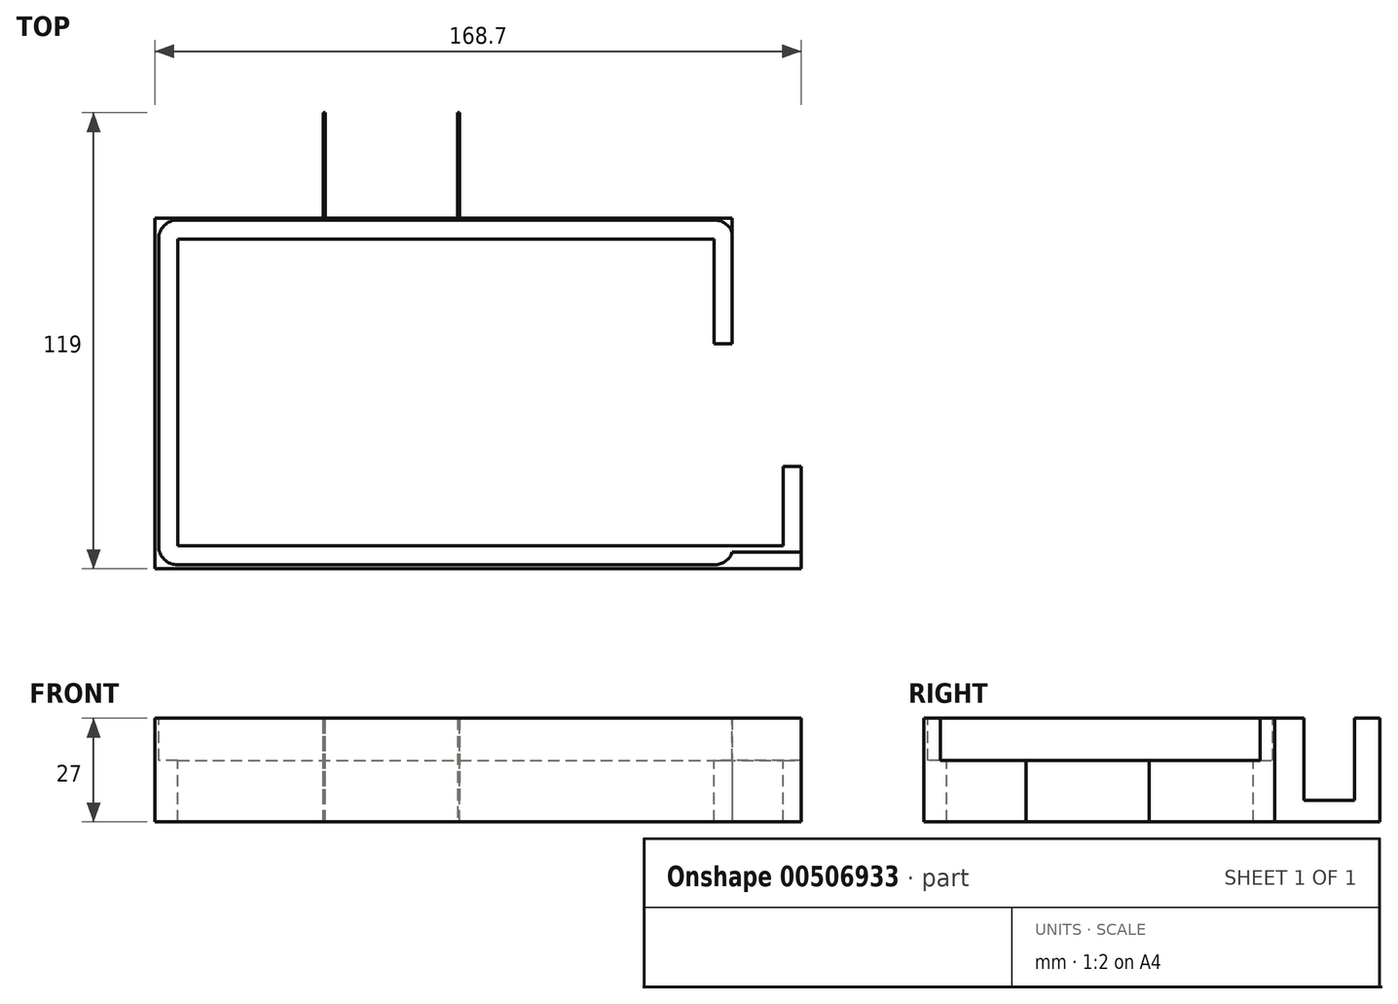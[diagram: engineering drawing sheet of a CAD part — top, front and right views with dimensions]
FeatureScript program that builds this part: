
annotation { "Feature Type Name" : "Feature", "Feature Type Description" : "" }
export const myFeature = defineFeature(function(context is Context, id is Id, definition is map)
    precondition{}
    {
        {
            var Q0;
            Q0=qCreatedBy(makeId("Top.planeOp"),FACE);
            var sketch = newSketch(context, id + "F0", { "sketchPlane" : qUnion([Q0])});
            skLineSegment(sketch, "E0.bottom", {"start": v(-95.15, 61.25) * mm, "end": v(74.85, 61.25) * mm});
            skLineSegment(sketch, "E0.top", {"start": v(-95.15, -68.75) * mm, "end": v(74.85, -68.75) * mm});
            skLineSegment(sketch, "E0.left", {"start": v(-95.15, 61.25) * mm, "end": v(-95.15, -68.75) * mm});
            skLineSegment(sketch, "E0.right", {"start": v(74.85, 61.25) * mm, "end": v(74.85, -68.75) * mm});
            skSolve(sketch);
        }
        {
            var Q0;
            Q0=makeQuery(id+"F0.imprint","IMPRINT",FACE,{"disambiguationData":[TD([[makeQuery(id+"F0.imprint","IMPRINT",EDGE,{"derivedFrom":sQuery(id+"F0.wireOp",EDGE,"E0.bottom")}),-1.0]])]});
            extrude(context, id + "F1", {"entities" : qUnion([Q0]), "depth" : 34 * mm});
        }
        {
            var Q0;
            Q0=makeQuery(id+"F1.opExtrude","CAP_FACE",FACE,{"disambiguationData":[OSD([sQuery(id+"F0.wireOp",EDGE,"E0.bottom"),sQuery(id+"F0.wireOp",EDGE,"E0.top"),sQuery(id+"F0.wireOp",EDGE,"E0.left"),sQuery(id+"F0.wireOp",EDGE,"E0.right")])],"isStart":false});
            shell(context, id + "F2", {"entities" : qUnion([Q0]), "thickness" : 1 * mm});
        }
        {
            var Q0;
            Q0=makeQuery(id+"F2.opShell","OFFSET_FACE",FACE,{"disambiguationData":[OSD([sQuery(id+"F0.wireOp",EDGE,"E0.bottom"),sQuery(id+"F0.wireOp",EDGE,"E0.top"),sQuery(id+"F0.wireOp",EDGE,"E0.left"),sQuery(id+"F0.wireOp",EDGE,"E0.right")])]});
            var sketch = newSketch(context, id + "F3", { "sketchPlane" : qUnion([Q0])});
            skLineSegment(sketch, "E1.bottom", {"start": v(-94.15, 60.25) * mm, "end": v(-50.65, 60.25) * mm});
            skLineSegment(sketch, "E1.top", {"start": v(-94.15, 22.25) * mm, "end": v(-50.65, 22.25) * mm});
            skLineSegment(sketch, "E1.left", {"start": v(-94.15, 60.25) * mm, "end": v(-94.15, 22.25) * mm});
            skLineSegment(sketch, "E1.right", {"start": v(-50.65, 60.25) * mm, "end": v(-50.65, 22.25) * mm});
            skSolve(sketch);
        }
        {
            var Q0;
            Q0=makeQuery(id+"F3.imprint","IMPRINT",FACE,{"disambiguationData":[TD([[makeQuery(id+"F3.imprint","IMPRINT",EDGE,{"derivedFrom":sQuery(id+"F3.wireOp",EDGE,"E1.bottom")}),-1.0]])]});
            extrude(context, id + "F4", {"entities" : qUnion([Q0]), "operationType" : NewBodyOperationType.ADD, "depth" : 32 * mm});
        }
        {
            var Q0;
            Q0=makeQuery(id+"F4.opExtrude","CAP_FACE",FACE,{"disambiguationData":[OSD([sQuery(id+"F3.wireOp",EDGE,"E1.bottom"),sQuery(id+"F3.wireOp",EDGE,"E1.top"),sQuery(id+"F3.wireOp",EDGE,"E1.left"),sQuery(id+"F3.wireOp",EDGE,"E1.right")])],"isStart":false});
            shell(context, id + "F5", {"entities" : qUnion([Q0]), "thickness" : 0.5 * mm});
        }
        {
            var Q0;
            Q0=makeQuery(id+"F2.opShell","OFFSET_FACE",FACE,{"disambiguationData":[OSD([sQuery(id+"F0.wireOp",EDGE,"E0.bottom"),sQuery(id+"F0.wireOp",EDGE,"E0.top"),sQuery(id+"F0.wireOp",EDGE,"E0.left"),sQuery(id+"F0.wireOp",EDGE,"E0.right")])]});
            var sketch = newSketch(context, id + "F6", { "sketchPlane" : qUnion([Q0])});
            skLineSegment(sketch, "E2.bottom", {"start": v(-50.65, 22.25) * mm, "end": v(-15.65, 22.25) * mm});
            skLineSegment(sketch, "E2.top", {"start": v(-50.65, 60.25) * mm, "end": v(-15.65, 60.25) * mm});
            skLineSegment(sketch, "E2.left", {"start": v(-50.65, 22.25) * mm, "end": v(-50.65, 60.25) * mm});
            skLineSegment(sketch, "E2.right", {"start": v(-15.65, 22.25) * mm, "end": v(-15.65, 60.25) * mm});
            skSolve(sketch);
        }
        {
            var Q0;
            Q0=makeQuery(id+"F6.imprint","IMPRINT",FACE,{"disambiguationData":[TD([[makeQuery(id+"F6.imprint","IMPRINT",EDGE,{"derivedFrom":sQuery(id+"F6.wireOp",EDGE,"E2.bottom")}),1.0]])]});
            extrude(context, id + "F7", {"entities" : qUnion([Q0]), "operationType" : NewBodyOperationType.ADD, "depth" : 32 * mm});
        }
        {
            var Q0;
            Q0=makeQuery(id+"F7.boolean.opBoolean","MERGE",FACE,{"derivedFrom":[makeQuery(id+"F4.opExtrude","CAP_FACE",FACE,{"disambiguationData":[OSD([sQuery(id+"F3.wireOp",EDGE,"E1.bottom"),sQuery(id+"F3.wireOp",EDGE,"E1.top"),sQuery(id+"F3.wireOp",EDGE,"E1.left"),sQuery(id+"F3.wireOp",EDGE,"E1.right")])],"isStart":false}),makeQuery(id+"F7.opExtrude","CAP_FACE",FACE,{"disambiguationData":[OSD([sQuery(id+"F6.wireOp",EDGE,"E2.bottom"),sQuery(id+"F6.wireOp",EDGE,"E2.top"),sQuery(id+"F6.wireOp",EDGE,"E2.left"),sQuery(id+"F6.wireOp",EDGE,"E2.right")])],"isStart":false})]});
            shell(context, id + "F8", {"entities" : qUnion([Q0]), "thickness" : 0.5 * mm});
        }
        {
            var Q0;
            Q0=makeQuery(id+"F2.opShell","OFFSET_FACE",FACE,{"disambiguationData":[OSD([sQuery(id+"F0.wireOp",EDGE,"E0.bottom"),sQuery(id+"F0.wireOp",EDGE,"E0.top"),sQuery(id+"F0.wireOp",EDGE,"E0.left"),sQuery(id+"F0.wireOp",EDGE,"E0.right")])]});
            var sketch = newSketch(context, id + "F9", { "sketchPlane" : qUnion([Q0])});
            skLineSegment(sketch, "E3.bottom", {"start": v(-15.65, 22.25) * mm, "end": v(73.85, 22.25) * mm});
            skLineSegment(sketch, "E3.top", {"start": v(-15.65, 60.25) * mm, "end": v(73.85, 60.25) * mm});
            skLineSegment(sketch, "E3.left", {"start": v(-15.65, 22.25) * mm, "end": v(-15.65, 60.25) * mm});
            skLineSegment(sketch, "E3.right", {"start": v(73.85, 22.25) * mm, "end": v(73.85, 60.25) * mm});
            skSolve(sketch);
        }
        {
            var Q0;
            Q0=makeQuery(id+"F9.imprint","IMPRINT",FACE,{"disambiguationData":[TD([[makeQuery(id+"F9.imprint","IMPRINT",EDGE,{"derivedFrom":sQuery(id+"F9.wireOp",EDGE,"E3.bottom")}),1.0]])]});
            extrude(context, id + "F10", {"entities" : qUnion([Q0]), "operationType" : NewBodyOperationType.ADD, "depth" : 32 * mm});
        }
        {
            var Q0;
            Q0=makeQuery(id+"F10.boolean.opBoolean","MERGE",FACE,{"derivedFrom":[makeQuery(id+"F7.boolean.opBoolean","MERGE",FACE,{"derivedFrom":[makeQuery(id+"F4.opExtrude","CAP_FACE",FACE,{"disambiguationData":[OSD([sQuery(id+"F3.wireOp",EDGE,"E1.bottom"),sQuery(id+"F3.wireOp",EDGE,"E1.top"),sQuery(id+"F3.wireOp",EDGE,"E1.left"),sQuery(id+"F3.wireOp",EDGE,"E1.right")])],"isStart":false}),makeQuery(id+"F7.opExtrude","CAP_FACE",FACE,{"disambiguationData":[OSD([sQuery(id+"F6.wireOp",EDGE,"E2.bottom"),sQuery(id+"F6.wireOp",EDGE,"E2.top"),sQuery(id+"F6.wireOp",EDGE,"E2.left"),sQuery(id+"F6.wireOp",EDGE,"E2.right")])],"isStart":false})]}),makeQuery(id+"F10.opExtrude","CAP_FACE",FACE,{"disambiguationData":[OSD([sQuery(id+"F9.wireOp",EDGE,"E3.bottom"),sQuery(id+"F9.wireOp",EDGE,"E3.top"),sQuery(id+"F9.wireOp",EDGE,"E3.left"),sQuery(id+"F9.wireOp",EDGE,"E3.right")])],"isStart":false})]});
            shell(context, id + "F11", {"entities" : qUnion([Q0]), "thickness" : 0.5 * mm});
        }
        {
            var Q0;
            Q0=makeQuery(id+"F2.opShell","OFFSET_FACE",FACE,{"disambiguationData":[OSD([sQuery(id+"F0.wireOp",EDGE,"E0.bottom"),sQuery(id+"F0.wireOp",EDGE,"E0.top"),sQuery(id+"F0.wireOp",EDGE,"E0.left"),sQuery(id+"F0.wireOp",EDGE,"E0.right")])]});
            var sketch = newSketch(context, id + "F12", { "sketchPlane" : qUnion([Q0])});
            skLineSegment(sketch, "E4.bottom", {"start": v(-94.15, -67.75) * mm, "end": v(55.85, -67.75) * mm});
            skLineSegment(sketch, "E4.top", {"start": v(-94.15, 22.25) * mm, "end": v(55.85, 22.25) * mm});
            skLineSegment(sketch, "E4.left", {"start": v(-94.15, -67.75) * mm, "end": v(-94.15, 22.25) * mm});
            skLineSegment(sketch, "E4.right", {"start": v(55.85, -67.75) * mm, "end": v(55.85, 22.25) * mm});
            skSolve(sketch);
        }
        {
            var Q0;
            Q0=makeQuery(id+"F12.imprint","IMPRINT",FACE,{"disambiguationData":[TD([[makeQuery(id+"F12.imprint","IMPRINT",EDGE,{"derivedFrom":sQuery(id+"F12.wireOp",EDGE,"E4.bottom")}),1.0]])]});
            extrude(context, id + "F13", {"entities" : qUnion([Q0]), "operationType" : NewBodyOperationType.ADD, "depth" : 32 * mm});
        }
        {
            var Q0;
            Q0=makeQuery(id+"F13.opExtrude","CAP_FACE",FACE,{"disambiguationData":[OSD([sQuery(id+"F12.wireOp",EDGE,"E4.bottom"),sQuery(id+"F12.wireOp",EDGE,"E4.top"),sQuery(id+"F12.wireOp",EDGE,"E4.left"),sQuery(id+"F12.wireOp",EDGE,"E4.right")])],"isStart":false});
            var sketch = newSketch(context, id + "F14", { "sketchPlane" : qUnion([Q0])});
            skLineSegment(sketch, "E5.bottom", {"start": v(-89.15, 22.25) * mm, "end": v(50.85, 22.25) * mm});
            skLineSegment(sketch, "E5.top", {"start": v(-89.15, -67.75) * mm, "end": v(50.85, -67.75) * mm});
            skLineSegment(sketch, "E5.left", {"start": v(-94.15, 17.25) * mm, "end": v(-94.15, -62.75) * mm});
            skLineSegment(sketch, "E5.right", {"start": v(55.85, 17.25) * mm, "end": v(55.85, -62.75) * mm});
            skPoint(sketch, "E6.visualSharp", {"position": v(-94.15, 22.25) * mm});
            skArc(sketch, "E6.filletArc", {"start": v(-89.15, 22.25) * mm, "mid": v(-92.68, 20.79) * mm, "end": v(-94.15, 17.25) * mm});
            skPoint(sketch, "E7.visualSharp", {"position": v(55.85, 22.25) * mm});
            skArc(sketch, "E7.filletArc", {"start": v(55.85, 17.25) * mm, "mid": v(54.39, 20.79) * mm, "end": v(50.85, 22.25) * mm});
            skPoint(sketch, "E8.visualSharp", {"position": v(55.85, -67.75) * mm});
            skArc(sketch, "E8.filletArc", {"start": v(50.85, -67.75) * mm, "mid": v(54.39, -66.28) * mm, "end": v(55.85, -62.75) * mm});
            skPoint(sketch, "E9.visualSharp", {"position": v(-94.15, -67.75) * mm});
            skArc(sketch, "E9.filletArc", {"start": v(-94.15, -62.75) * mm, "mid": v(-92.68, -66.28) * mm, "end": v(-89.15, -67.75) * mm});
            skSolve(sketch);
        }
        {
            var Q0;
            Q0=makeQuery(id+"F14.imprint","IMPRINT",FACE,{"disambiguationData":[TD([[makeQuery(id+"F14.imprint","IMPRINT",EDGE,{"derivedFrom":sQuery(id+"F14.wireOp",EDGE,"E5.bottom")}),-1.0]])]});
            extrude(context, id + "F15", {"entities" : qUnion([Q0]), "operationType" : NewBodyOperationType.REMOVE, "oppositeDirection" : true, "depth" : 17 * mm});
        }
        {
            var Q0;
            Q0=makeQuery(id+"F15.boolean.opBoolean","COPY",FACE,{"derivedFrom":makeQuery(id+"F15.opExtrude","CAP_FACE",FACE,{"disambiguationData":[OSD([sQuery(id+"F14.wireOp",EDGE,"E5.bottom"),sQuery(id+"F14.wireOp",EDGE,"E5.top"),sQuery(id+"F14.wireOp",EDGE,"E5.left"),sQuery(id+"F14.wireOp",EDGE,"E5.right"),sQuery(id+"F14.wireOp",EDGE,"E7.filletArc"),sQuery(id+"F14.wireOp",EDGE,"E8.filletArc"),sQuery(id+"F14.wireOp",EDGE,"E6.filletArc"),sQuery(id+"F14.wireOp",EDGE,"E9.filletArc")])],"isStart":false})});
            var sketch = newSketch(context, id + "F16", { "sketchPlane" : qUnion([Q0])});
            skLineSegment(sketch, "E10.bottom", {"start": v(-89.15, 17.25) * mm, "end": v(50.85, 17.25) * mm});
            skLineSegment(sketch, "E10.top", {"start": v(-89.15, -62.75) * mm, "end": v(50.85, -62.75) * mm});
            skLineSegment(sketch, "E10.left", {"start": v(-89.15, 17.25) * mm, "end": v(-89.15, -62.75) * mm});
            skLineSegment(sketch, "E10.right", {"start": v(50.85, 17.25) * mm, "end": v(50.85, -62.75) * mm});
            skSolve(sketch);
        }
        {
            var Q0;
            Q0=makeQuery(id+"F16.imprint","IMPRINT",FACE,{"disambiguationData":[TD([[makeQuery(id+"F16.imprint","IMPRINT",EDGE,{"derivedFrom":sQuery(id+"F16.wireOp",EDGE,"E10.bottom")}),-1.0]])]});
            extrude(context, id + "F17", {"entities" : qUnion([Q0]), "operationType" : NewBodyOperationType.REMOVE, "oppositeDirection" : true, "depth" : 25 * mm});
        }
        {
            var Q0;
            Q0=makeQuery(id+"F5.opShell","OFFSET_FACE",FACE,{"disambiguationData":[OSD([sQuery(id+"F0.wireOp",EDGE,"E0.bottom"),sQuery(id+"F0.wireOp",EDGE,"E0.top"),sQuery(id+"F0.wireOp",EDGE,"E0.left"),sQuery(id+"F0.wireOp",EDGE,"E0.right")])]});
            extrude(context, id + "F18", {"entities" : qUnion([Q0]), "operationType" : NewBodyOperationType.REMOVE, "oppositeDirection" : true, "depth" : 25 * mm});
        }
        {
            var Q0;
            Q0=makeQuery(id+"F8.opShell","OFFSET_FACE",FACE,{"disambiguationData":[OSD([sQuery(id+"F0.wireOp",EDGE,"E0.bottom"),sQuery(id+"F0.wireOp",EDGE,"E0.top"),sQuery(id+"F0.wireOp",EDGE,"E0.left"),sQuery(id+"F0.wireOp",EDGE,"E0.right")])]});
            extrude(context, id + "F19", {"entities" : qUnion([Q0]), "operationType" : NewBodyOperationType.REMOVE, "oppositeDirection" : true, "depth" : 25 * mm});
        }
        {
            var Q0;
            Q0=makeQuery(id+"F11.opShell","OFFSET_FACE",FACE,{"disambiguationData":[OSD([sQuery(id+"F0.wireOp",EDGE,"E0.bottom"),sQuery(id+"F0.wireOp",EDGE,"E0.top"),sQuery(id+"F0.wireOp",EDGE,"E0.left"),sQuery(id+"F0.wireOp",EDGE,"E0.right")])]});
            extrude(context, id + "F20", {"entities" : qUnion([Q0]), "operationType" : NewBodyOperationType.REMOVE, "oppositeDirection" : true, "depth" : 25 * mm});
        }
        {
            var Q0;
            Q0=makeQuery(id+"F2.opShell","OFFSET_FACE",FACE,{"disambiguationData":[OSD([sQuery(id+"F0.wireOp",EDGE,"E0.bottom"),sQuery(id+"F0.wireOp",EDGE,"E0.top"),sQuery(id+"F0.wireOp",EDGE,"E0.left"),sQuery(id+"F0.wireOp",EDGE,"E0.right")])]});
            extrude(context, id + "F21", {"entities" : qUnion([Q0]), "operationType" : NewBodyOperationType.REMOVE, "oppositeDirection" : true, "depth" : 25 * mm});
        }
        {
            var Q0;
            {var subQ0=sQuery(id+"F9.wireOp",EDGE,"E3.bottom");var subQ1=sQuery(id+"F6.wireOp",EDGE,"E2.bottom");var subQ2=sQuery(id+"F3.wireOp",EDGE,"E1.top");Q0=makeQuery(id+"F21.boolean.opBoolean","MERGE",FACE,{"derivedFrom":[makeQuery(id+"F10.boolean.opBoolean","MERGE",FACE,{"derivedFrom":[makeQuery(id+"F7.boolean.opBoolean","MERGE",FACE,{"derivedFrom":[makeQuery(id+"F4.opExtrude","SWEPT_FACE",FACE,{"disambiguationData":[OSD([subQ2])]}),makeQuery(id+"F7.opExtrude","SWEPT_FACE",FACE,{"disambiguationData":[OSD([subQ1])]})]}),makeQuery(id+"F10.opExtrude","SWEPT_FACE",FACE,{"disambiguationData":[OSD([subQ0])]})]}),makeQuery(id+"F21.opExtrude","SWEPT_FACE",FACE,{"disambiguationData":[OSD([subQ2,subQ1,subQ0])]})]});}
            var sketch = newSketch(context, id + "F22", { "sketchPlane" : qUnion([Q0])});
            skLineSegment(sketch, "E11", {"start": v(-87.7, 33) * mm, "end": v(-87.7, 0) * mm});
            skLineSegment(sketch, "E12", {"start": v(-69.73, 33) * mm, "end": v(-69.73, 0) * mm});
            skLineSegment(sketch, "E13", {"start": v(-40.47, 33) * mm, "end": v(-40.47, 0) * mm});
            skLineSegment(sketch, "E14", {"start": v(-23.84, 33) * mm, "end": v(-23.84, 0) * mm});
            skLineSegment(sketch, "E15", {"start": v(0, 33) * mm, "end": v(0, 0) * mm});
            skLineSegment(sketch, "E16", {"start": v(34.73, 33) * mm, "end": v(34.73, 0) * mm});
            skLineSegment(sketch, "E17", {"start": v(-87.7, 5.75) * mm, "end": v(73.85, 4.23) * mm});
            skSolve(sketch);
        }
        {
            var Q0;
            {var subQ0=sQuery(id+"F22.wireOp",EDGE,"E11");var subQ3=sQuery(id+"F22.wireOp",EDGE,"E17");var subQ4=makeQuery(id+"F22.imprint","INTERSECT",VERTEX,{"derivedFrom":[subQ0,subQ3]});Q0=makeQuery(id+"F22.imprint","IMPRINT",FACE,{"disambiguationData":[TD([[makeQuery(id+"F22.imprint","IMPRINT",EDGE,{"disambiguationData":[TD([[subQ4,-1.0]])],"derivedFrom":subQ3}),1.0]])]});}
            var Q1;
            {var subQ0=sQuery(id+"F22.wireOp",EDGE,"E13");var subQ3=sQuery(id+"F22.wireOp",EDGE,"E17");var subQ4=makeQuery(id+"F22.imprint","INTERSECT",VERTEX,{"derivedFrom":[subQ0,subQ3]});Q1=makeQuery(id+"F22.imprint","IMPRINT",FACE,{"disambiguationData":[TD([[makeQuery(id+"F22.imprint","IMPRINT",EDGE,{"disambiguationData":[TD([[subQ4,-1.0]])],"derivedFrom":subQ3}),1.0]])]});}
            var Q2;
            {var subQ0=sQuery(id+"F22.wireOp",EDGE,"E15");var subQ3=sQuery(id+"F22.wireOp",EDGE,"E17");var subQ4=makeQuery(id+"F22.imprint","INTERSECT",VERTEX,{"derivedFrom":[subQ0,subQ3]});Q2=makeQuery(id+"F22.imprint","IMPRINT",FACE,{"disambiguationData":[TD([[makeQuery(id+"F22.imprint","IMPRINT",EDGE,{"disambiguationData":[TD([[subQ4,-1.0]])],"derivedFrom":subQ3}),1.0]])]});}
            extrude(context, id + "F23", {"entities" : qUnion([Q0, Q1, Q2]), "operationType" : NewBodyOperationType.REMOVE, "depth" : 25 * mm, "hasSecondDirection" : true, "secondDirectionOppositeDirection" : true, "secondDirectionDepth" : 25 * mm});
        }
        {
            var Q0;
            Q0=makeQuery(id+"F1.opExtrude","SWEPT_FACE",FACE,{"disambiguationData":[OSD([sQuery(id+"F0.wireOp",EDGE,"E0.bottom")])]});
            var sketch = newSketch(context, id + "F24", { "sketchPlane" : qUnion([Q0])});
            skLineSegment(sketch, "E18.bottom", {"start": v(-74.85, 0) * mm, "end": v(95.15, 0) * mm});
            skLineSegment(sketch, "E18.top", {"start": v(-74.85, 34) * mm, "end": v(95.15, 34) * mm});
            skLineSegment(sketch, "E18.left", {"start": v(-74.85, 0) * mm, "end": v(-74.85, 34) * mm});
            skLineSegment(sketch, "E18.right", {"start": v(95.15, 0) * mm, "end": v(95.15, 34) * mm});
            skSolve(sketch);
        }
        {
            var Q0;
            Q0=makeQuery(id+"F24.imprint","IMPRINT",FACE,{"disambiguationData":[TD([[makeQuery(id+"F24.imprint","IMPRINT",EDGE,{"derivedFrom":sQuery(id+"F24.wireOp",EDGE,"E18.bottom")}),-1.0]])]});
            extrude(context, id + "F25", {"entities" : qUnion([Q0]), "operationType" : NewBodyOperationType.REMOVE, "oppositeDirection" : true, "depth" : 11 * mm});
        }
        {
            var Q0;
            Q0=makeQuery(id+"F1.opExtrude","SWEPT_FACE",FACE,{"disambiguationData":[OSD([sQuery(id+"F0.wireOp",EDGE,"E0.right")])]});
            var sketch = newSketch(context, id + "F26", { "sketchPlane" : qUnion([Q0])});
            skLineSegment(sketch, "E19.bottom", {"start": v(-68.75, 0) * mm, "end": v(50.25, 0) * mm});
            skLineSegment(sketch, "E19.top", {"start": v(-68.75, 34) * mm, "end": v(50.25, 34) * mm});
            skLineSegment(sketch, "E19.left", {"start": v(-68.75, 0) * mm, "end": v(-68.75, 34) * mm});
            skLineSegment(sketch, "E19.right", {"start": v(50.25, 0) * mm, "end": v(50.25, 34) * mm});
            skSolve(sketch);
        }
        {
            var Q0;
            Q0=makeQuery(id+"F26.imprint","IMPRINT",FACE,{"disambiguationData":[TD([[makeQuery(id+"F26.imprint","IMPRINT",EDGE,{"derivedFrom":sQuery(id+"F26.wireOp",EDGE,"E19.bottom")}),-1.0]])]});
            extrude(context, id + "F27", {"entities" : qUnion([Q0]), "operationType" : NewBodyOperationType.REMOVE, "oppositeDirection" : true, "depth" : 19.3 * mm});
        }
        {
            var Q0;
            Q0=makeQuery(id+"F27.boolean.opBoolean","COPY",FACE,{"derivedFrom":makeQuery(id+"F27.opExtrude","CAP_FACE",FACE,{"disambiguationData":[OSD([sQuery(id+"F26.wireOp",EDGE,"E19.bottom"),sQuery(id+"F26.wireOp",EDGE,"E19.top"),sQuery(id+"F26.wireOp",EDGE,"E19.left"),sQuery(id+"F26.wireOp",EDGE,"E19.right")])],"isStart":false})});
            var sketch = newSketch(context, id + "F28", { "sketchPlane" : qUnion([Q0])});
            skLineSegment(sketch, "E20", {"start": v(-42.1, 16) * mm, "end": v(-42.1, 0) * mm});
            skLineSegment(sketch, "E21", {"start": v(-10, 16) * mm, "end": v(-10, 0) * mm});
            skSolve(sketch);
        }
        {
            var Q0;
            {var subQ0=sQuery(id+"F28.wireOp",EDGE,"E20");Q0=makeQuery(id+"F28.imprint","IMPRINT",FACE,{"disambiguationData":[TD([[makeQuery(id+"F28.imprint","IMPRINT",EDGE,{"derivedFrom":subQ0}),1.0]])]});}
            extrude(context, id + "F29", {"entities" : qUnion([Q0]), "operationType" : NewBodyOperationType.REMOVE, "oppositeDirection" : true, "depth" : 25 * mm});
        }
        {
            var Q0;
            Q0=makeQuery(id+"F1.opExtrude","SWEPT_FACE",FACE,{"disambiguationData":[OSD([sQuery(id+"F0.wireOp",EDGE,"E0.left")])]});
            var sketch = newSketch(context, id + "F30", { "sketchPlane" : qUnion([Q0])});
            skLineSegment(sketch, "E22.bottom", {"start": v(-43.7, 34) * mm, "end": v(-30.4, 34) * mm});
            skLineSegment(sketch, "E22.top", {"start": v(-43.7, 5.56) * mm, "end": v(-30.4, 5.56) * mm});
            skLineSegment(sketch, "E22.left", {"start": v(-43.7, 34) * mm, "end": v(-43.7, 5.56) * mm});
            skLineSegment(sketch, "E22.right", {"start": v(-30.4, 34) * mm, "end": v(-30.4, 5.56) * mm});
            skSolve(sketch);
        }
        {
            var Q0;
            Q0=makeQuery(id+"F30.imprint","IMPRINT",FACE,{"disambiguationData":[TD([[makeQuery(id+"F30.imprint","IMPRINT",EDGE,{"derivedFrom":sQuery(id+"F30.wireOp",EDGE,"E22.bottom")}),-1.0]])]});
            extrude(context, id + "F31", {"entities" : qUnion([Q0]), "operationType" : NewBodyOperationType.REMOVE, "oppositeDirection" : true, "depth" : 96.3 * mm});
        }
        {
            var Q0;
            {var subQ0=sQuery(id+"F0.wireOp",EDGE,"E0.left");var subQ1=sQuery(id+"F0.wireOp",EDGE,"E0.top");Q0=makeQuery(id+"F31.boolean.opBoolean","SPLIT",FACE,{"disambiguationData":[TD([makeQuery(id+"F1.opExtrude","SWEPT_FACE",FACE,{"disambiguationData":[OSD([subQ1])]})])],"derivedFrom":makeQuery(id+"F1.opExtrude","CAP_FACE",FACE,{"disambiguationData":[OSD([sQuery(id+"F0.wireOp",EDGE,"E0.bottom"),subQ1,subQ0,sQuery(id+"F0.wireOp",EDGE,"E0.right")])],"isStart":false})});}
            var sketch = newSketch(context, id + "F32", { "sketchPlane" : qUnion([Q0])});
            skLineSegment(sketch, "E23.bottom", {"start": v(-104.4, -98.73) * mm, "end": v(132.33, -98.73) * mm});
            skLineSegment(sketch, "E23.top", {"start": v(-104.4, 100.46) * mm, "end": v(132.33, 100.46) * mm});
            skLineSegment(sketch, "E23.left", {"start": v(-104.4, -98.73) * mm, "end": v(-104.4, 100.46) * mm});
            skLineSegment(sketch, "E23.right", {"start": v(132.33, -98.73) * mm, "end": v(132.33, 100.46) * mm});
            skSolve(sketch);
        }
        {
            var Q0;
            Q0 = qSketchRegion(id + "F32", true);
            extrude(context, id + "F33", {"entities" : qUnion([Q0]), "operationType" : NewBodyOperationType.REMOVE, "oppositeDirection" : true, "depth" : 7 * mm});
        }
        {
            var Q0;
            {var subQ2=sQuery(id+"F0.wireOp",EDGE,"E0.top");Q0=makeQuery(id+"F29.boolean.opBoolean","SPLIT",FACE,{"disambiguationData":[TD([makeQuery(id+"F1.opExtrude","SWEPT_FACE",FACE,{"disambiguationData":[OSD([subQ2])]})])],"derivedFrom":makeQuery(id+"F27.boolean.opBoolean","COPY",FACE,{"derivedFrom":makeQuery(id+"F27.opExtrude","CAP_FACE",FACE,{"disambiguationData":[OSD([sQuery(id+"F26.wireOp",EDGE,"E19.bottom"),sQuery(id+"F26.wireOp",EDGE,"E19.top"),sQuery(id+"F26.wireOp",EDGE,"E19.left"),sQuery(id+"F26.wireOp",EDGE,"E19.right")])],"isStart":false})})});}
            extrude(context, id + "F34", {"entities" : qUnion([Q0]), "operationType" : NewBodyOperationType.ADD, "depth" : 18 * mm});
        }
        {
            var Q0;
            Q0=makeQuery(id+"F29.boolean.opBoolean","SPLIT",FACE,{"disambiguationData":[TD([makeQuery(id+"F17.boolean.opBoolean","COPY",FACE,{"derivedFrom":makeQuery(id+"F17.opExtrude","SWEPT_FACE",FACE,{"disambiguationData":[OSD([sQuery(id+"F16.wireOp",EDGE,"E10.top")])]})})])],"derivedFrom":makeQuery(id+"F17.boolean.opBoolean","COPY",FACE,{"derivedFrom":makeQuery(id+"F17.opExtrude","SWEPT_FACE",FACE,{"disambiguationData":[OSD([sQuery(id+"F16.wireOp",EDGE,"E10.right")])]})})});
            extrude(context, id + "F35", {"entities" : qUnion([Q0]), "operationType" : NewBodyOperationType.REMOVE, "oppositeDirection" : true, "depth" : 18 * mm});
        }
        {
            var Q0;
            {var subQ0=sQuery(id+"F0.wireOp",EDGE,"E0.left");Q0=makeQuery(id+"F25.boolean.opBoolean","COPY",FACE,{"disambiguationData":[TD([makeQuery(id+"F1.opExtrude","SWEPT_FACE",FACE,{"disambiguationData":[OSD([subQ0])]})])],"derivedFrom":makeQuery(id+"F25.opExtrude","CAP_FACE",FACE,{"disambiguationData":[OSD([sQuery(id+"F24.wireOp",EDGE,"E18.bottom"),sQuery(id+"F24.wireOp",EDGE,"E18.top"),sQuery(id+"F24.wireOp",EDGE,"E18.left"),sQuery(id+"F24.wireOp",EDGE,"E18.right")])],"isStart":false})});}
            extrude(context, id + "F36", {"entities" : qUnion([Q0]), "operationType" : NewBodyOperationType.REMOVE, "oppositeDirection" : true, "depth" : 27.5 * mm});
        }
    });
